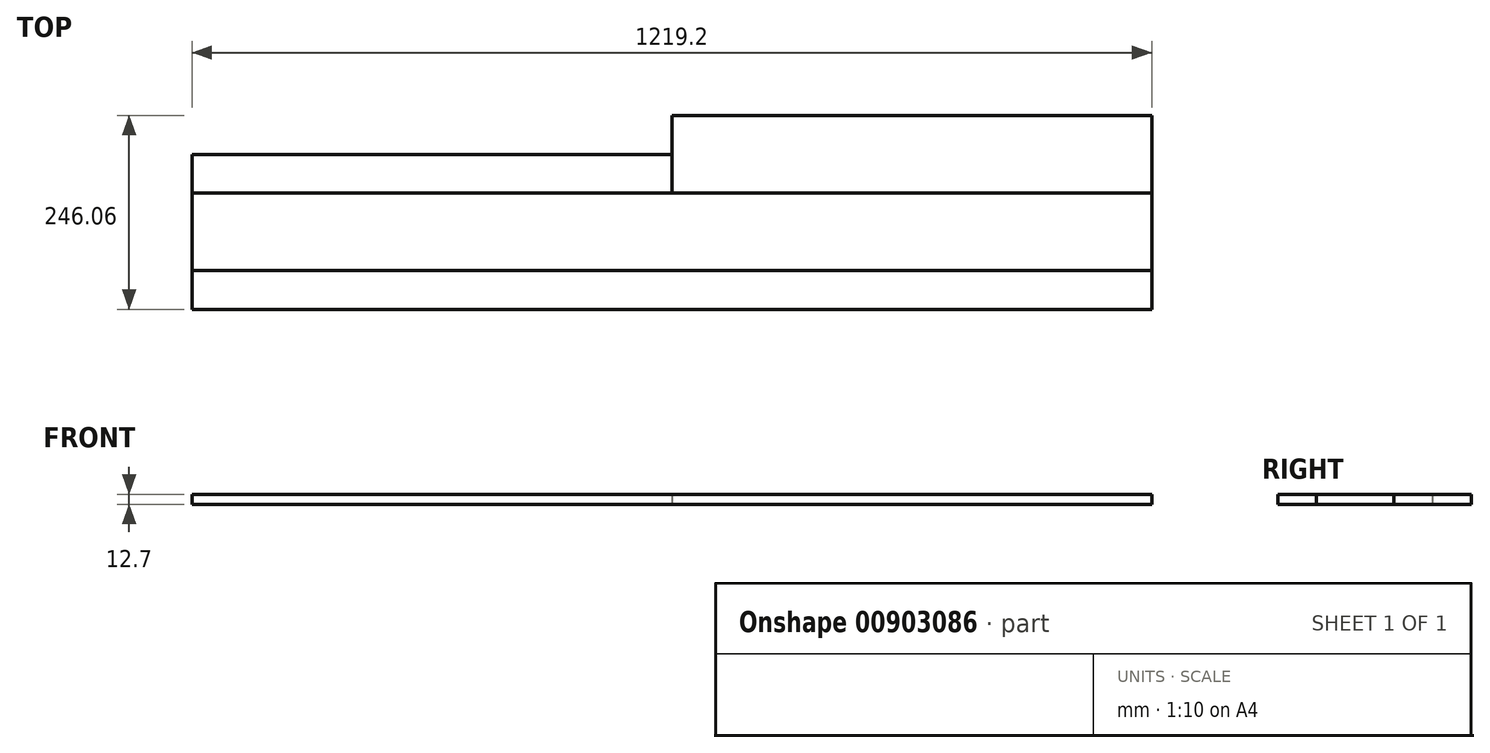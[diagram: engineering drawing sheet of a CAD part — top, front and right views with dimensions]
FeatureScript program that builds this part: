
annotation { "Feature Type Name" : "Feature", "Feature Type Description" : "" }
export const myFeature = defineFeature(function(context is Context, id is Id, definition is map)
    precondition{}
    {
        {
            var Q0;
            Q0=qCreatedBy(makeId("Top.planeOp"),FACE);
            var sketch = newSketch(context, id + "F0", { "sketchPlane" : qUnion([Q0])});
            skLineSegment(sketch, "E0.bottom", {"start": v(0, 0) * mm, "end": v(1219.2, 0) * mm});
            skLineSegment(sketch, "E0.top", {"start": v(0, -98.43) * mm, "end": v(1219.2, -98.43) * mm});
            skLineSegment(sketch, "E0.left", {"start": v(0, 0) * mm, "end": v(0, -98.43) * mm});
            skLineSegment(sketch, "E0.right", {"start": v(1219.2, 0) * mm, "end": v(1219.2, -98.42) * mm});
            skSolve(sketch);
        }
        {
            var Q0;
            Q0 = qSketchRegion(id + "F0", true);
            extrude(context, id + "F1", {"entities" : qUnion([Q0]), "depth" : 12.7 * mm, "offsetDistance" : 25.4 * mm});
        }
        {
            var Q0;
            Q0=makeQuery(id+"F1.opExtrude","SWEPT_FACE",FACE,{"disambiguationData":[OSD([sQuery(id+"F0.wireOp",EDGE,"E0.top")])]});
            var sketch = newSketch(context, id + "F2", { "sketchPlane" : qUnion([Q0])});
            skLineSegment(sketch, "E1.bottom", {"start": v(0, 0) * mm, "end": v(1219.2, 0) * mm});
            skLineSegment(sketch, "E1.top", {"start": v(0, 12.7) * mm, "end": v(1219.2, 12.7) * mm});
            skLineSegment(sketch, "E1.left", {"start": v(0, 0) * mm, "end": v(0, 12.7) * mm});
            skLineSegment(sketch, "E1.right", {"start": v(1219.2, 0) * mm, "end": v(1219.2, 12.7) * mm});
            skSolve(sketch);
        }
        {
            var Q0;
            Q0 = qSketchRegion(id + "F2", true);
            extrude(context, id + "F3", {"entities" : qUnion([Q0]), "depth" : 49.2 * mm, "offsetDistance" : 25.4 * mm});
        }
        {
            var Q0;
            Q0=makeQuery(id+"F1.opExtrude","SWEPT_FACE",FACE,{"disambiguationData":[OSD([sQuery(id+"F0.wireOp",EDGE,"E0.bottom")])]});
            var sketch = newSketch(context, id + "F4", { "sketchPlane" : qUnion([Q0])});
            skLineSegment(sketch, "E2.bottom", {"start": v(-1219.2, 12.7) * mm, "end": v(-609.6, 12.7) * mm});
            skLineSegment(sketch, "E2.top", {"start": v(-1219.2, 0) * mm, "end": v(-609.6, 0) * mm});
            skLineSegment(sketch, "E2.left", {"start": v(-1219.2, 12.7) * mm, "end": v(-1219.2, 0) * mm});
            skLineSegment(sketch, "E2.right", {"start": v(-609.6, 12.7) * mm, "end": v(-609.6, 0) * mm});
            skSolve(sketch);
        }
        {
            var Q0;
            Q0 = qSketchRegion(id + "F4", true);
            extrude(context, id + "F5", {"entities" : qUnion([Q0]), "depth" : 98.42 * mm, "offsetDistance" : 25.4 * mm});
        }
        {
            var Q0;
            Q0=makeQuery(id+"F1.opExtrude","SWEPT_FACE",FACE,{"disambiguationData":[OSD([sQuery(id+"F0.wireOp",EDGE,"E0.bottom")])]});
            var sketch = newSketch(context, id + "F6", { "sketchPlane" : qUnion([Q0])});
            skLineSegment(sketch, "E3.bottom", {"start": v(0, 0) * mm, "end": v(-609.6, 0) * mm});
            skLineSegment(sketch, "E3.top", {"start": v(0, 12.7) * mm, "end": v(-609.6, 12.7) * mm});
            skLineSegment(sketch, "E3.left", {"start": v(0, 0) * mm, "end": v(0, 12.7) * mm});
            skLineSegment(sketch, "E3.right", {"start": v(-609.6, 0) * mm, "end": v(-609.6, 12.7) * mm});
            skSolve(sketch);
        }
        {
            var Q0;
            Q0 = qSketchRegion(id + "F6", true);
            extrude(context, id + "F7", {"entities" : qUnion([Q0]), "depth" : 49.2 * mm, "offsetDistance" : 25.4 * mm});
        }
    });
